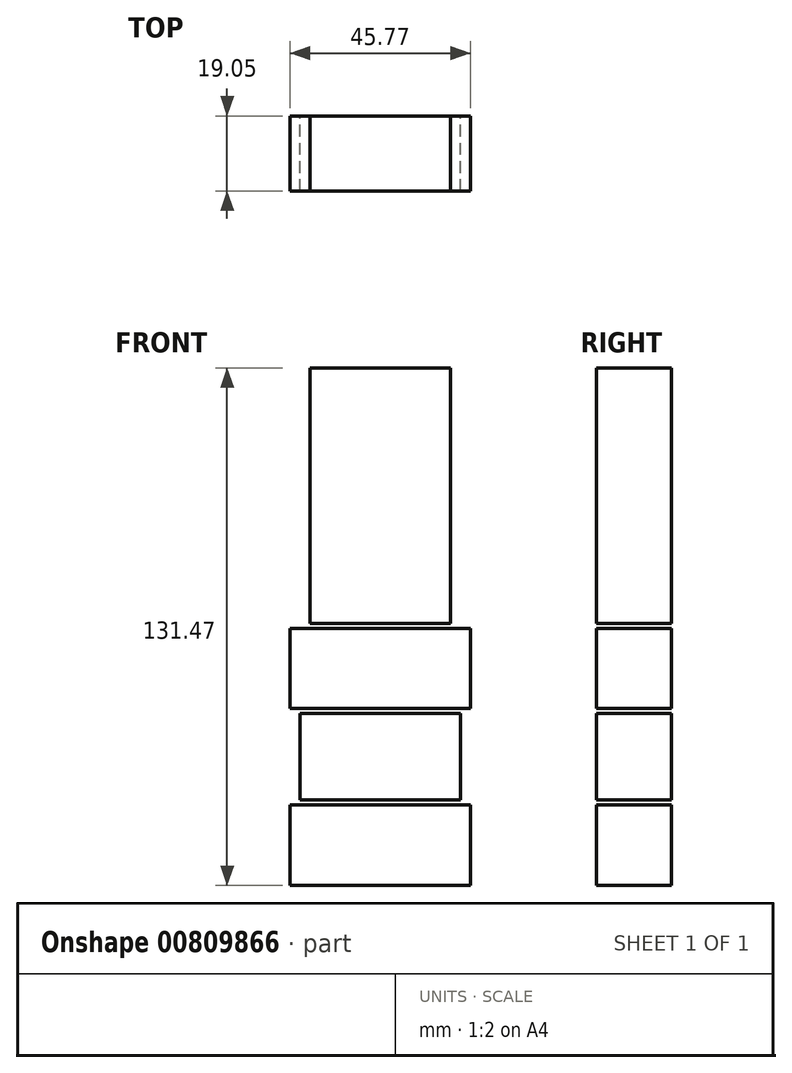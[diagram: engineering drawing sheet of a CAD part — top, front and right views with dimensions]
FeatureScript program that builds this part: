
annotation { "Feature Type Name" : "Feature", "Feature Type Description" : "" }
export const myFeature = defineFeature(function(context is Context, id is Id, definition is map)
    precondition{}
    {
        {
            var Q0;
            Q0=qCreatedBy(makeId("Front.planeOp"),FACE);
            var sketch = newSketch(context, id + "F0", { "sketchPlane" : qUnion([Q0])});
            skLineSegment(sketch, "E0.bottom", {"start": v(0, 0) * mm, "end": v(45.77, 0) * mm});
            skLineSegment(sketch, "E0.top", {"start": v(0, 20.5) * mm, "end": v(45.77, 20.5) * mm});
            skLineSegment(sketch, "E0.left", {"start": v(0, 0) * mm, "end": v(0, 20.5) * mm});
            skLineSegment(sketch, "E0.right", {"start": v(45.77, 0) * mm, "end": v(45.77, 20.5) * mm});
            skLineSegment(sketch, "E1.bottom", {"start": v(2.55, 21.77) * mm, "end": v(43.22, 21.77) * mm});
            skLineSegment(sketch, "E1.top", {"start": v(2.55, 43.74) * mm, "end": v(43.22, 43.74) * mm});
            skLineSegment(sketch, "E1.left", {"start": v(2.55, 21.77) * mm, "end": v(2.55, 43.74) * mm});
            skLineSegment(sketch, "E1.right", {"start": v(43.22, 21.77) * mm, "end": v(43.22, 43.74) * mm});
            skLineSegment(sketch, "E2.bottom", {"start": v(0, 45) * mm, "end": v(45.77, 45) * mm});
            skLineSegment(sketch, "E2.top", {"start": v(0, 65.33) * mm, "end": v(45.77, 65.33) * mm});
            skLineSegment(sketch, "E2.left", {"start": v(0, 45) * mm, "end": v(0, 65.33) * mm});
            skLineSegment(sketch, "E2.right", {"start": v(45.77, 45) * mm, "end": v(45.77, 65.33) * mm});
            skLineSegment(sketch, "E3.bottom", {"start": v(5.07, 66.6) * mm, "end": v(40.7, 66.6) * mm});
            skLineSegment(sketch, "E3.top", {"start": v(5.07, 131.47) * mm, "end": v(40.7, 131.47) * mm});
            skLineSegment(sketch, "E3.left", {"start": v(5.07, 66.6) * mm, "end": v(5.07, 131.47) * mm});
            skLineSegment(sketch, "E3.right", {"start": v(40.7, 66.6) * mm, "end": v(40.7, 131.47) * mm});
            skPoint(sketch, "E4", {"position": v(22.89, 0) * mm});
            skPoint(sketch, "E5", {"position": v(22.89, 21.77) * mm});
            skPoint(sketch, "E6", {"position": v(22.89, 45) * mm});
            skPoint(sketch, "E7", {"position": v(22.89, 66.6) * mm});
            skLineSegment(sketch, "E8", {"start": v(22.89, 0) * mm, "end": v(22.89, 138.5) * mm, "construction": true});
            skSolve(sketch);
        }
        {
            var Q0;
            Q0=makeQuery(id+"F0.imprint","IMPRINT",FACE,{"disambiguationData":[TD([[makeQuery(id+"F0.imprint","IMPRINT",EDGE,{"derivedFrom":sQuery(id+"F0.wireOp",EDGE,"E0.bottom")}),1.0]])]});
            var Q1;
            Q1=makeQuery(id+"F0.imprint","IMPRINT",FACE,{"disambiguationData":[TD([[makeQuery(id+"F0.imprint","IMPRINT",EDGE,{"derivedFrom":sQuery(id+"F0.wireOp",EDGE,"E1.bottom")}),1.0]])]});
            var Q2;
            Q2=makeQuery(id+"F0.imprint","IMPRINT",FACE,{"disambiguationData":[TD([[makeQuery(id+"F0.imprint","IMPRINT",EDGE,{"derivedFrom":sQuery(id+"F0.wireOp",EDGE,"E2.bottom")}),1.0]])]});
            var Q3;
            Q3=makeQuery(id+"F0.imprint","IMPRINT",FACE,{"disambiguationData":[TD([[makeQuery(id+"F0.imprint","IMPRINT",EDGE,{"derivedFrom":sQuery(id+"F0.wireOp",EDGE,"E3.bottom")}),1.0]])]});
            extrude(context, id + "F1", {"entities" : qUnion([Q0, Q1, Q2, Q3]), "depth" : 19.05 * mm, "offsetDistance" : 25.4 * mm});
        }
    });
